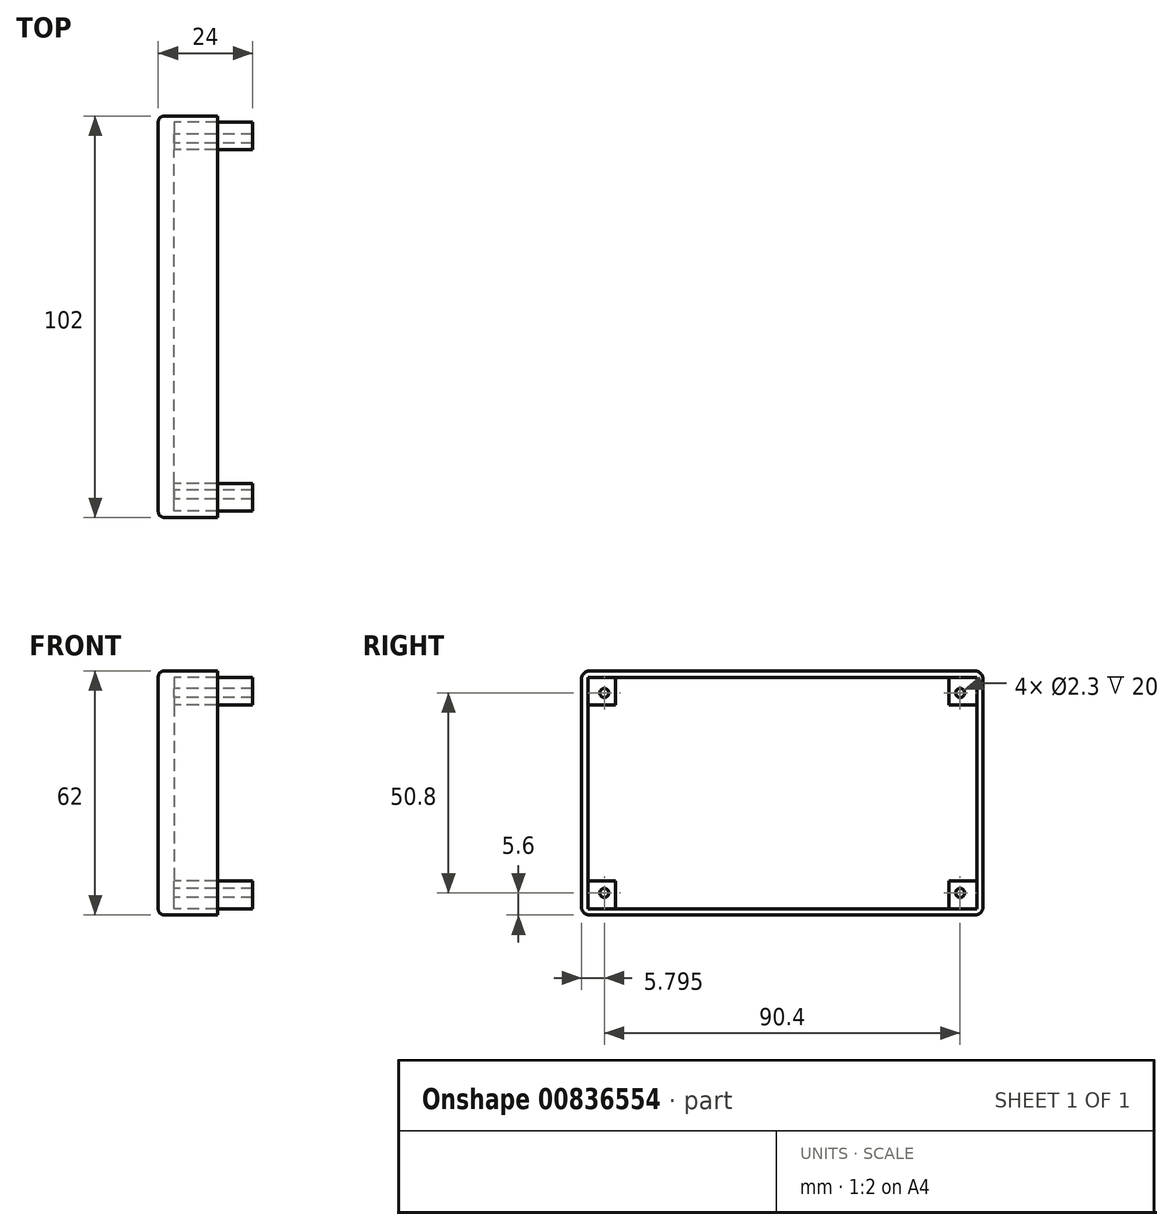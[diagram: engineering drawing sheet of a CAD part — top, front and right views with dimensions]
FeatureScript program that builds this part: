
annotation { "Feature Type Name" : "Feature", "Feature Type Description" : "" }
export const myFeature = defineFeature(function(context is Context, id is Id, definition is map)
    precondition{}
    {
        {
            var Q0;
            Q0=qCreatedBy(makeId("Right.planeOp"),FACE);
            var sketch = newSketch(context, id + "F0", { "sketchPlane" : qUnion([Q0])});
            skLineSegment(sketch, "E0.bottom", {"start": v(44.02, -30.5) * mm, "end": v(-57.98, -30.5) * mm});
            skLineSegment(sketch, "E0.top", {"start": v(44.02, 31.5) * mm, "end": v(-57.98, 31.5) * mm});
            skLineSegment(sketch, "E0.left", {"start": v(44.02, -30.5) * mm, "end": v(44.02, 31.5) * mm});
            skLineSegment(sketch, "E0.right", {"start": v(-57.98, -30.5) * mm, "end": v(-57.98, 31.5) * mm});
            skSolve(sketch);
        }
        {
            var Q0;
            Q0=makeQuery(id+"F0.imprint","IMPRINT",FACE,{"disambiguationData":[TD([[makeQuery(id+"F0.imprint","IMPRINT",EDGE,{"derivedFrom":sQuery(id+"F0.wireOp",EDGE,"E0.bottom")}),-1.0]])]});
            extrude(context, id + "F1", {"entities" : qUnion([Q0]), "depth" : -15 * mm, "offsetDistance" : 25 * mm});
        }
        {
            var Q0;
            Q0=makeQuery(id+"F1.opExtrude","CAP_EDGE",EDGE,{"disambiguationData":[OSD([sQuery(id+"F0.wireOp",EDGE,"E0.top")])],"isStart":false});
            var Q1;
            Q1=makeQuery(id+"F1.opExtrude","CAP_EDGE",EDGE,{"disambiguationData":[OSD([sQuery(id+"F0.wireOp",EDGE,"E0.right")])],"isStart":false});
            var Q2;
            Q2=makeQuery(id+"F1.opExtrude","CAP_EDGE",EDGE,{"disambiguationData":[OSD([sQuery(id+"F0.wireOp",EDGE,"E0.bottom")])],"isStart":false});
            var Q3;
            Q3=makeQuery(id+"F1.opExtrude","CAP_EDGE",EDGE,{"disambiguationData":[OSD([sQuery(id+"F0.wireOp",EDGE,"E0.left")])],"isStart":false});
            fillet(context, id + "F2", {"entities" : qUnion([Q0, Q1, Q2, Q3]), "radius" : 1.5 * mm, "tangentPropagation" : true, "allowEdgeOverflow" : false});
        }
        {
            var Q0;
            Q0=makeQuery(id+"F1.opExtrude","CAP_FACE",FACE,{"disambiguationData":[OSD([sQuery(id+"F0.wireOp",EDGE,"E0.bottom"),sQuery(id+"F0.wireOp",EDGE,"E0.top"),sQuery(id+"F0.wireOp",EDGE,"E0.left"),sQuery(id+"F0.wireOp",EDGE,"E0.right"),sQuery(id+"F0.wireOp",EDGE,"4fae5d3a-a934-4e2d-86fe-7a198d1b89ea"),sQuery(id+"F0.wireOp",EDGE,"31228899-52bc-47af-9744-5eedbbe198bb"),sQuery(id+"F0.wireOp",EDGE,"2778fd41-0ab7-436f-a2e2-faf06f34bb3f"),sQuery(id+"F0.wireOp",EDGE,"aaa3216f-0535-4fce-bf30-473ebea8b936")])],"isStart":true});
            var sketch = newSketch(context, id + "F3", { "sketchPlane" : qUnion([Q0])});
            skLineSegment(sketch, "E1.bottom", {"start": v(-56.38, 29.9) * mm, "end": v(42.42, 29.9) * mm});
            skLineSegment(sketch, "E1.top", {"start": v(-56.38, -28.9) * mm, "end": v(42.42, -28.9) * mm});
            skLineSegment(sketch, "E1.left", {"start": v(-56.38, 29.9) * mm, "end": v(-56.38, -28.9) * mm});
            skLineSegment(sketch, "E1.right", {"start": v(42.42, 29.9) * mm, "end": v(42.42, -28.9) * mm});
            skSolve(sketch);
        }
        {
            var Q0;
            Q0=makeQuery(id+"F3.imprint","IMPRINT",FACE,{"disambiguationData":[TD([[makeQuery(id+"F3.imprint","IMPRINT",EDGE,{"derivedFrom":sQuery(id+"F3.wireOp",EDGE,"E1.bottom")}),-1.0]])]});
            extrude(context, id + "F4", {"entities" : qUnion([Q0]), "operationType" : NewBodyOperationType.REMOVE, "oppositeDirection" : true, "depth" : 11 * mm, "offsetDistance" : 25 * mm});
        }
        {
            var Q0;
            Q0=makeQuery(id+"F4.boolean.opBoolean","COPY",FACE,{"derivedFrom":makeQuery(id+"F4.opExtrude","CAP_FACE",FACE,{"disambiguationData":[OSD([sQuery(id+"F0.wireOp",EDGE,"4fae5d3a-a934-4e2d-86fe-7a198d1b89ea"),sQuery(id+"F0.wireOp",EDGE,"31228899-52bc-47af-9744-5eedbbe198bb"),sQuery(id+"F0.wireOp",EDGE,"2778fd41-0ab7-436f-a2e2-faf06f34bb3f"),sQuery(id+"F0.wireOp",EDGE,"aaa3216f-0535-4fce-bf30-473ebea8b936"),sQuery(id+"F3.wireOp",EDGE,"E1.bottom"),sQuery(id+"F3.wireOp",EDGE,"E1.top"),sQuery(id+"F3.wireOp",EDGE,"E1.left"),sQuery(id+"F3.wireOp",EDGE,"E1.right")])],"isStart":false})});
            var sketch = newSketch(context, id + "F5", { "sketchPlane" : qUnion([Q0])});
            skLineSegment(sketch, "E2.bottom", {"start": v(-56.38, -28.9) * mm, "end": v(-49.38, -28.9) * mm});
            skLineSegment(sketch, "E2.top", {"start": v(-56.38, -21.9) * mm, "end": v(-49.38, -21.9) * mm});
            skLineSegment(sketch, "E2.left", {"start": v(-56.38, -28.9) * mm, "end": v(-56.38, -21.9) * mm});
            skLineSegment(sketch, "E2.right", {"start": v(-49.38, -28.9) * mm, "end": v(-49.38, -21.9) * mm});
            skLineSegment(sketch, "E3.bottom", {"start": v(42.42, -28.9) * mm, "end": v(35.42, -28.9) * mm});
            skLineSegment(sketch, "E3.top", {"start": v(42.42, -21.9) * mm, "end": v(35.42, -21.9) * mm});
            skLineSegment(sketch, "E3.left", {"start": v(42.42, -28.9) * mm, "end": v(42.42, -21.9) * mm});
            skLineSegment(sketch, "E3.right", {"start": v(35.42, -28.9) * mm, "end": v(35.42, -21.9) * mm});
            skLineSegment(sketch, "E4.bottom", {"start": v(42.42, 29.9) * mm, "end": v(35.42, 29.9) * mm});
            skLineSegment(sketch, "E4.top", {"start": v(42.42, 22.9) * mm, "end": v(35.42, 22.9) * mm});
            skLineSegment(sketch, "E4.left", {"start": v(42.42, 29.9) * mm, "end": v(42.42, 22.9) * mm});
            skLineSegment(sketch, "E4.right", {"start": v(35.42, 29.9) * mm, "end": v(35.42, 22.9) * mm});
            skLineSegment(sketch, "E5.bottom", {"start": v(-56.38, 29.9) * mm, "end": v(-49.38, 29.9) * mm});
            skLineSegment(sketch, "E5.top", {"start": v(-56.38, 22.9) * mm, "end": v(-49.38, 22.9) * mm});
            skLineSegment(sketch, "E5.left", {"start": v(-56.38, 29.9) * mm, "end": v(-56.38, 22.9) * mm});
            skLineSegment(sketch, "E5.right", {"start": v(-49.38, 29.9) * mm, "end": v(-49.38, 22.9) * mm});
            skCircle(sketch, "E6", {"center": v(-52.18, -24.9) * mm, "radius": 1.15 * mm});
            skCircle(sketch, "E7", {"center": v(-52.18, 25.9) * mm, "radius": 1.15 * mm});
            skCircle(sketch, "E8", {"center": v(38.22, 25.9) * mm, "radius": 1.15 * mm});
            skCircle(sketch, "E9", {"center": v(38.22, -24.9) * mm, "radius": 1.15 * mm});
            skSolve(sketch);
        }
        {
            var Q0;
            {var subQ1=sQuery(id+"F5.wireOp",EDGE,"5co9mj8w-vUKV-g5V8-X10N-qeDsRfb8O3eS.left");Q0=makeQuery(id+"F5.imprint","IMPRINT",FACE,{"disambiguationData":[TD([[makeQuery(id+"F5.imprint","IMPRINT",EDGE,{"derivedFrom":subQ1}),-1.0]])]});}
            var Q1;
            {var subQ2=sQuery(id+"F5.wireOp",EDGE,"Yt5NghoU-M3ol-SGgZ-LCPh-5uIIVFkw0AUm.top");Q1=makeQuery(id+"F5.imprint","IMPRINT",FACE,{"disambiguationData":[TD([[makeQuery(id+"F5.imprint","IMPRINT",EDGE,{"derivedFrom":subQ2}),1.0]])]});}
            var Q2;
            {var subQ0=sQuery(id+"F5.wireOp",EDGE,"Yt5NghoU-M3ol-SGgZ-LCPh-5uIIVFkw0AUm.left");var subQ1=sQuery(id+"F5.wireOp",EDGE,"Yt5NghoU-M3ol-SGgZ-LCPh-5uIIVFkw0AUm.bottom");var subQ2=makeQuery(id+"F5.imprint","INTERSECT",VERTEX,{"derivedFrom":[subQ1,subQ0]});Q2=makeQuery(id+"F5.imprint","IMPRINT",FACE,{"disambiguationData":[TD([[makeQuery(id+"F5.imprint","IMPRINT",EDGE,{"disambiguationData":[TD([[subQ2,-1.0]])],"derivedFrom":subQ1}),-1.0]])]});}
            var Q3;
            Q3=makeQuery(id+"F5.imprint","IMPRINT",FACE,{"disambiguationData":[TD([[makeQuery(id+"F5.imprint","IMPRINT",EDGE,{"derivedFrom":sQuery(id+"F5.wireOp",EDGE,"E2.bottom")}),1.0]])]});
            var Q4;
            Q4=makeQuery(id+"F5.imprint","IMPRINT",FACE,{"disambiguationData":[TD([[makeQuery(id+"F5.imprint","IMPRINT",EDGE,{"derivedFrom":sQuery(id+"F5.wireOp",EDGE,"E3.bottom")}),-1.0]])]});
            var Q5;
            Q5=makeQuery(id+"F5.imprint","IMPRINT",FACE,{"disambiguationData":[TD([[makeQuery(id+"F5.imprint","IMPRINT",EDGE,{"derivedFrom":sQuery(id+"F5.wireOp",EDGE,"E4.bottom")}),1.0]])]});
            var Q6;
            Q6=makeQuery(id+"F5.imprint","IMPRINT",FACE,{"disambiguationData":[TD([[makeQuery(id+"F5.imprint","IMPRINT",EDGE,{"derivedFrom":sQuery(id+"F5.wireOp",EDGE,"E5.bottom")}),-1.0]])]});
            var Q7;
            Q7=makeQuery(id+"F5.imprint","IMPRINT",FACE,{"disambiguationData":[TD([[makeQuery(id+"F5.imprint","IMPRINT",EDGE,{"derivedFrom":sQuery(id+"F5.wireOp",EDGE,"E4.bottom")}),-1.0]])]});
            var Q8;
            Q8=makeQuery(id+"F5.imprint","IMPRINT",FACE,{"disambiguationData":[TD([[makeQuery(id+"F5.imprint","IMPRINT",EDGE,{"derivedFrom":sQuery(id+"F5.wireOp",EDGE,"E3.bottom")}),1.0]])]});
            extrude(context, id + "F6", {"entities" : qUnion([Q0, Q1, Q2, Q3, Q4, Q5, Q6, Q7, Q8]), "operationType" : NewBodyOperationType.ADD, "depth" : 20 * mm, "offsetDistance" : 25 * mm});
        }
        {
            var Q0;
            Q0=makeQuery(id+"F1.opExtrude","SWEPT_EDGE",EDGE,{"disambiguationData":[OSD([sQuery(id+"F0.wireOp",EDGE,"E0.bottom"),sQuery(id+"F0.wireOp",EDGE,"E0.right")])]});
            var Q1;
            Q1=makeQuery(id+"F1.opExtrude","SWEPT_EDGE",EDGE,{"disambiguationData":[OSD([sQuery(id+"F0.wireOp",EDGE,"E0.top"),sQuery(id+"F0.wireOp",EDGE,"E0.right")])]});
            var Q2;
            Q2=makeQuery(id+"F1.opExtrude","SWEPT_EDGE",EDGE,{"disambiguationData":[OSD([sQuery(id+"F0.wireOp",EDGE,"E0.top"),sQuery(id+"F0.wireOp",EDGE,"E0.left")])]});
            var Q3;
            Q3=makeQuery(id+"F1.opExtrude","SWEPT_EDGE",EDGE,{"disambiguationData":[OSD([sQuery(id+"F0.wireOp",EDGE,"E0.bottom"),sQuery(id+"F0.wireOp",EDGE,"E0.left")])]});
            fillet(context, id + "F7", {"entities" : qUnion([Q0, Q1, Q2, Q3]), "radius" : 2 * mm, "tangentPropagation" : true, "allowEdgeOverflow" : false});
        }
    });
